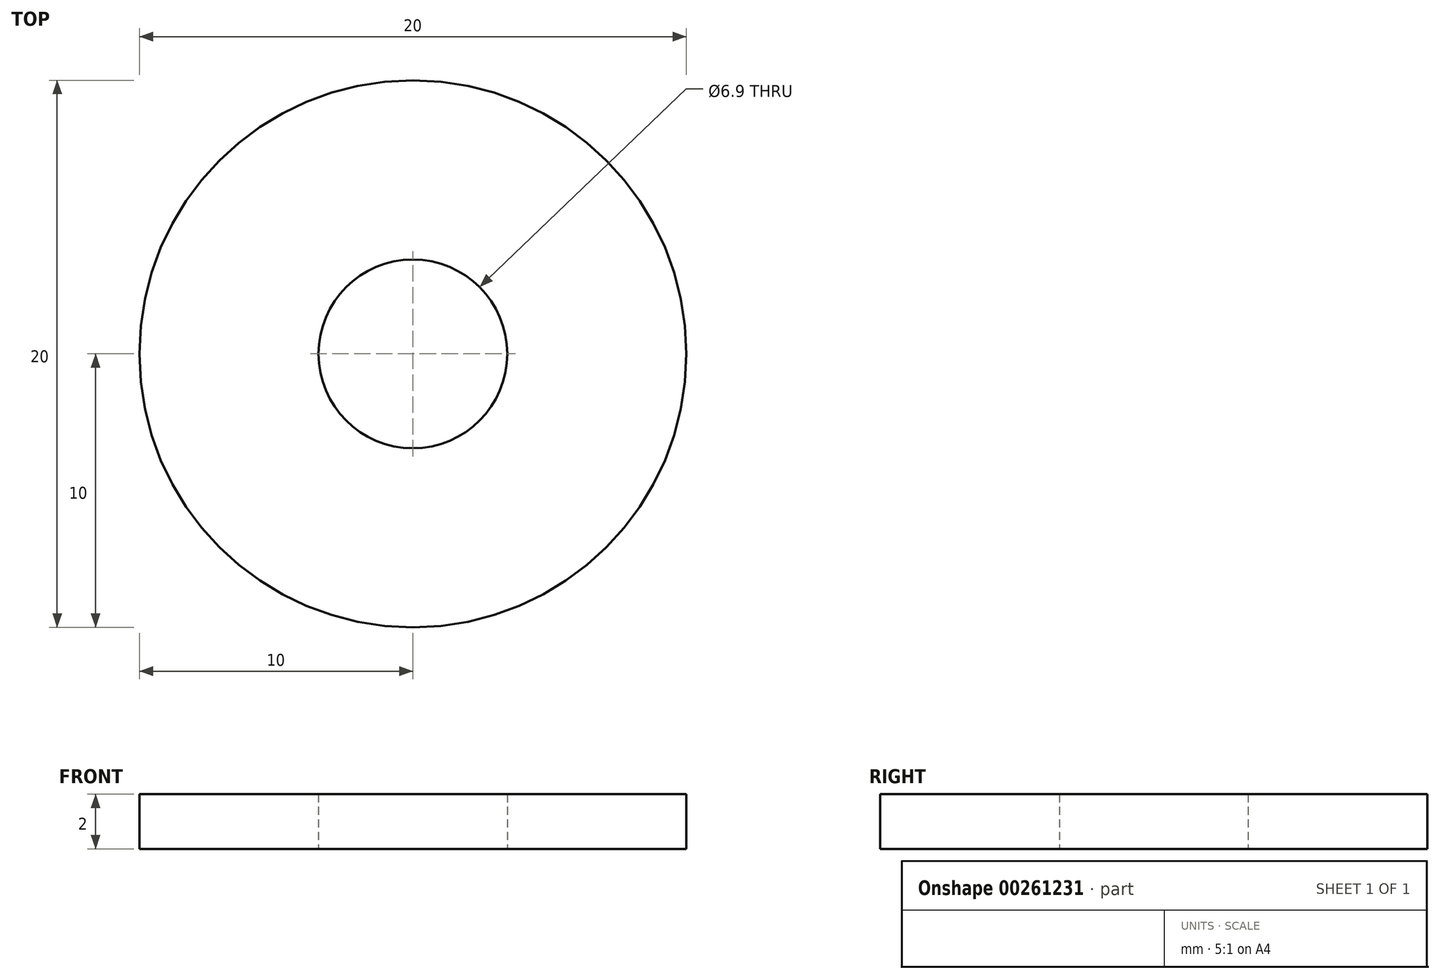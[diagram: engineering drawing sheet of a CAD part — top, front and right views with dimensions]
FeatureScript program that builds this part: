
annotation { "Feature Type Name" : "Feature", "Feature Type Description" : "" }
export const myFeature = defineFeature(function(context is Context, id is Id, definition is map)
    precondition{}
    {
        {
            var Q0;
            Q0=qCreatedBy(makeId("Top.planeOp"),FACE);
            var sketch = newSketch(context, id + "F0", { "sketchPlane" : qUnion([Q0])});
            skCircle(sketch, "E0", {"center": v(0, 0) * mm, "radius": 3.45 * mm});
            skCircle(sketch, "E1", {"center": v(0, 0) * mm, "radius": 10 * mm});
            skSolve(sketch);
        }
        {
            var Q0;
            Q0=makeQuery(id+"F0.imprint","IMPRINT",FACE,{"disambiguationData":[TD([[makeQuery(id+"F0.imprint","IMPRINT",EDGE,{"derivedFrom":sQuery(id+"F0.wireOp",EDGE,"E0")}),-1.0]])]});
            extrude(context, id + "F1", {"entities" : qUnion([Q0]), "depth" : 2 * mm});
        }
    });
